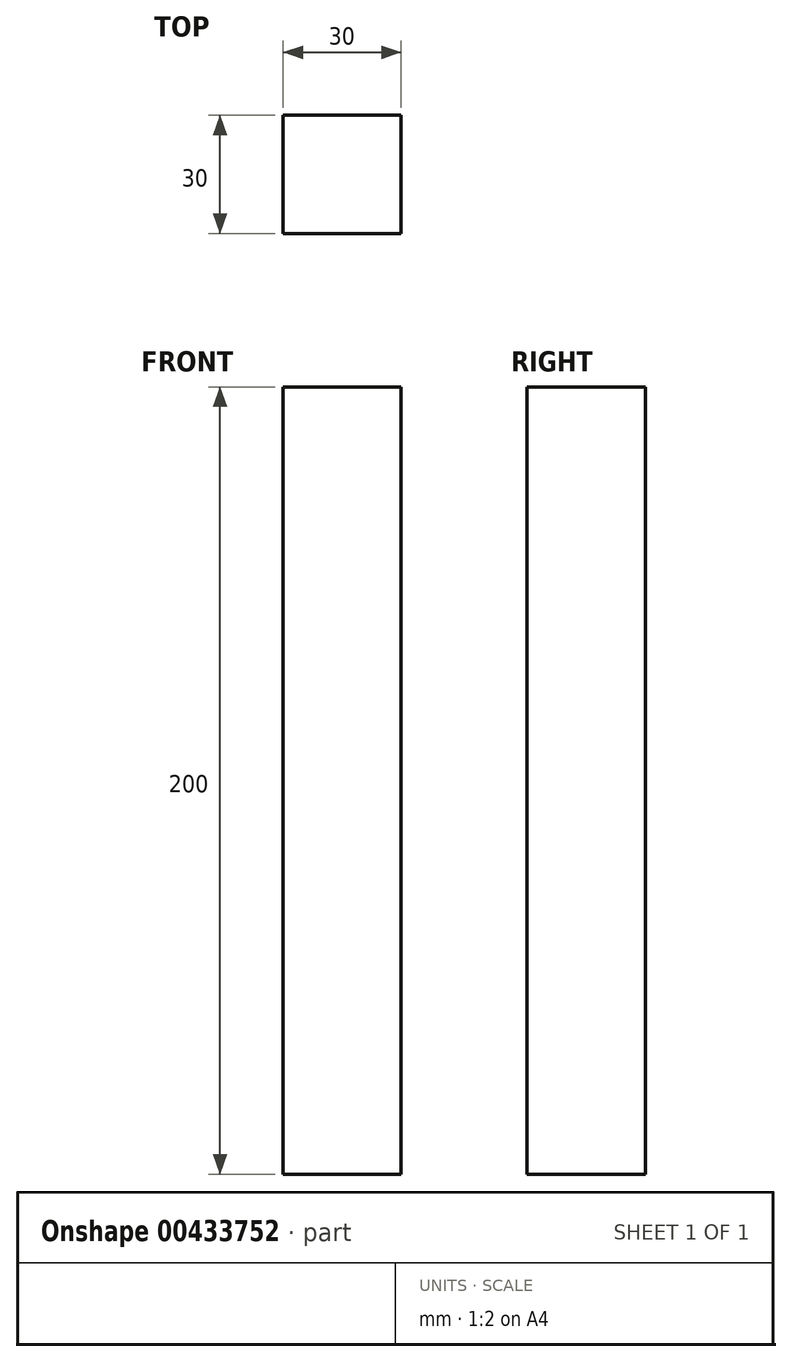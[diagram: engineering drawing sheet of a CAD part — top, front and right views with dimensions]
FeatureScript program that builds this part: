
annotation { "Feature Type Name" : "Feature", "Feature Type Description" : "" }
export const myFeature = defineFeature(function(context is Context, id is Id, definition is map)
    precondition{}
    {
        {
            var Q0;
            Q0=qCreatedBy(makeId("Front.planeOp"),FACE);
            var sketch = newSketch(context, id + "F0", { "sketchPlane" : qUnion([Q0])});
            skLineSegment(sketch, "E0.bottom", {"start": v(-39.7, 171.63) * mm, "end": v(-9.7, 171.63) * mm});
            skLineSegment(sketch, "E0.top", {"start": v(-39.7, -28.37) * mm, "end": v(-9.7, -28.37) * mm});
            skLineSegment(sketch, "E0.left", {"start": v(-39.7, 171.63) * mm, "end": v(-39.7, -28.37) * mm});
            skLineSegment(sketch, "E0.right", {"start": v(-9.7, 171.63) * mm, "end": v(-9.7, -28.37) * mm});
            skSolve(sketch);
        }
        {
            var Q0;
            Q0=makeQuery(id+"F0.imprint","IMPRINT",FACE,{"disambiguationData":[TD([[makeQuery(id+"F0.imprint","IMPRINT",EDGE,{"derivedFrom":sQuery(id+"F0.wireOp",EDGE,"E0.bottom")}),-1.0]])]});
            extrude(context, id + "F1", {"entities" : qUnion([Q0]), "depth" : 30 * mm, "offsetDistance" : 25 * mm});
        }
    });
